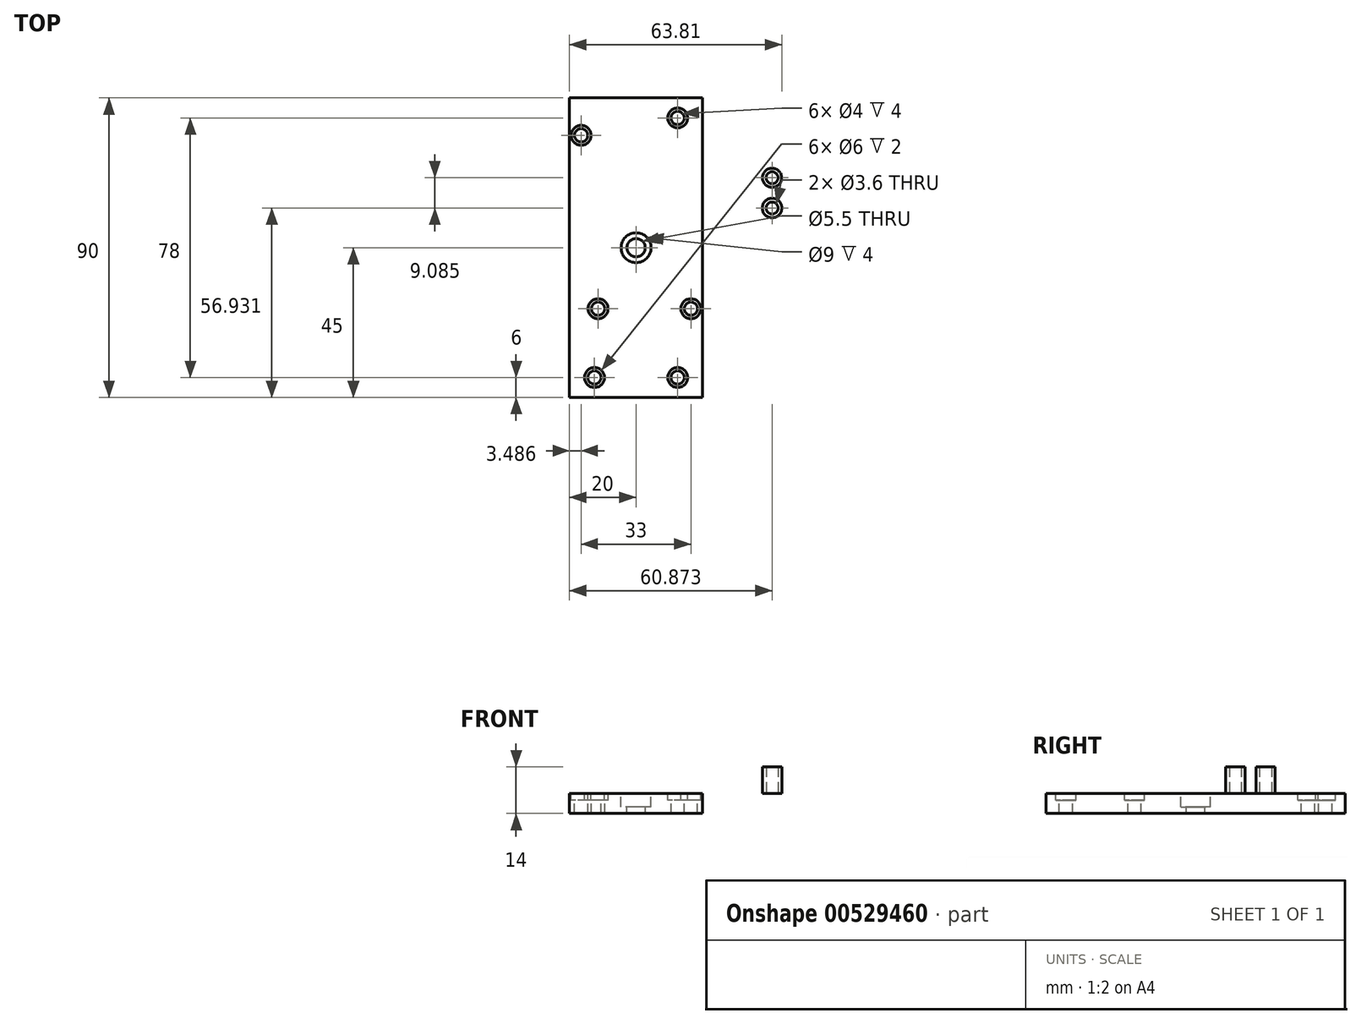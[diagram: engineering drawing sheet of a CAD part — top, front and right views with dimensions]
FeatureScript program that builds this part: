
annotation { "Feature Type Name" : "Feature", "Feature Type Description" : "" }
export const myFeature = defineFeature(function(context is Context, id is Id, definition is map)
    precondition{}
    {
        {
            assignVariable(context, id + "F0", {"name" : "base", "anyValue" : 6});
        }
        {
            assignVariable(context, id + "F1", {"name" : "pilar_d", "anyValue" : 6});
        }
        {
            var Q0;
            Q0=qCreatedBy(makeId("Top.planeOp"),FACE);
            var sketch = newSketch(context, id + "F2", { "sketchPlane" : qUnion([Q0])});
            skLineSegment(sketch, "E0.bottom", {"start": v(-20, 45) * mm, "end": v(20, 45) * mm});
            skLineSegment(sketch, "E0.top", {"start": v(-20, -45) * mm, "end": v(20, -45) * mm});
            skLineSegment(sketch, "E0.left", {"start": v(-20, 45) * mm, "end": v(-20, -45) * mm});
            skLineSegment(sketch, "E0.right", {"start": v(20, 45) * mm, "end": v(20, -45) * mm});
            skPoint(sketch, "E0.middle", {"position": v(0, 0) * mm});
            skLineSegment(sketch, "E1.bottom", {"start": v(12.5, 39) * mm, "end": v(-12.5, 39) * mm, "construction": true});
            skLineSegment(sketch, "E1.top", {"start": v(12.5, -39) * mm, "end": v(-12.5, -39) * mm, "construction": true});
            skLineSegment(sketch, "E1.left", {"start": v(12.5, 39) * mm, "end": v(12.5, -39) * mm, "construction": true});
            skLineSegment(sketch, "E1.right", {"start": v(-12.5, 39) * mm, "end": v(-12.5, -39) * mm, "construction": true});
            skLineSegment(sketch, "E2", {"start": v(-11.41, -18.33) * mm, "end": v(16.49, -18.33) * mm, "construction": true});
            skLineSegment(sketch, "E3", {"start": v(-11.41, -18.33) * mm, "end": v(-11.41, 33.77) * mm, "construction": true});
            skLineSegment(sketch, "E4", {"start": v(-11.41, 33.77) * mm, "end": v(-16.51, 33.77) * mm, "construction": true});
            skCircle(sketch, "E5", {"center": v(0, 0) * mm, "radius": 15 * mm});
            skCircle(sketch, "E6", {"center": v(40.87, 21.02) * mm, "radius": 2.88 * mm});
            skCircle(sketch, "E7", {"center": v(40.87, 11.93) * mm, "radius": 2.94 * mm});
            skLineSegment(sketch, "E8", {"start": v(40.87, 45.46) * mm, "end": v(40.87, -2.42) * mm, "construction": true});
            skSolve(sketch);
        }
        {
            var Q0;
            Q0=qCreatedBy(makeId("Top.planeOp"),FACE);
            var sketch = newSketch(context, id + "F3", { "sketchPlane" : qUnion([Q0])});
            skCircle(sketch, "E9", {"center": v(12.5, 39) * mm, "radius": 3 * mm});
            skCircle(sketch, "E10", {"center": v(12.5, -39) * mm, "radius": 3 * mm});
            skCircle(sketch, "E11", {"center": v(-12.5, -39) * mm, "radius": 3 * mm});
            skSolve(sketch);
        }
        {
            var Q0;
            Q0=qCreatedBy(makeId("Top.planeOp"),FACE);
            var sketch = newSketch(context, id + "F4", { "sketchPlane" : qUnion([Q0])});
            skCircle(sketch, "E12", {"center": v(16.49, -18.33) * mm, "radius": 3 * mm});
            skCircle(sketch, "E13", {"center": v(-11.41, -18.33) * mm, "radius": 3 * mm});
            skCircle(sketch, "E14", {"center": v(-16.51, 33.77) * mm, "radius": 3 * mm});
            skSolve(sketch);
        }
        {
            var Q0;
            Q0=makeQuery(id+"F2.imprint","IMPRINT",FACE,{"disambiguationData":[TD([[makeQuery(id+"F2.imprint","IMPRINT",EDGE,{"derivedFrom":sQuery(id+"F2.wireOp",EDGE,"E0.bottom")}),-1.0]])]});
            var Q1;
            Q1=makeQuery(id+"F2.imprint","IMPRINT",FACE,{"disambiguationData":[TD([[makeQuery(id+"F2.imprint","IMPRINT",EDGE,{"derivedFrom":sQuery(id+"F2.wireOp",EDGE,"E5")}),1.0]])]});
            extrude(context, id + "F5", {"entities" : qUnion([Q0, Q1]), "oppositeDirection" : true, "depth" : (getVariable(context, 'base')) * mm, "offsetDistance" : 25 * mm});
        }
        {
            var Q0;
            Q0=sQuery(id+"F2.wireOp",VERTEX,"E0.middle");
            var Q1;
            Q1=makeQuery(id+"F5.opExtrude","SWEPT_BODY",BODY,{"disambiguationData":[OSD([sQuery(id+"F2.wireOp",EDGE,"E0.bottom"),sQuery(id+"F2.wireOp",EDGE,"E0.top"),sQuery(id+"F2.wireOp",EDGE,"E0.left"),sQuery(id+"F2.wireOp",EDGE,"E0.right")])]});
            hole(context, id + "F6", {"style" : HoleStyle.C_BORE, "endStyle" : HoleEndStyle.BLIND, "holeDiameter" : 5.5 * mm, "cBoreDiameter" : 9 * mm, "cBoreDepth" : 4 * mm, "majorDiameter" : 5 * mm, "holeDepth" : 30 * mm, "isTappedThrough" : true, "tappedDepth" : 10.5 * mm, "tapClearance" : 3, "locations" : qUnion([Q0]), "scope" : qUnion([Q1])});
        }
        {
            var Q0;
            Q0=sQuery(id+"F2.wireOp",VERTEX,"E1.left.start");
            var Q1;
            Q1=sQuery(id+"F2.wireOp",VERTEX,"E4.end");
            var Q2;
            Q2=sQuery(id+"F4.wireOp",VERTEX,"E12.center");
            var Q3;
            Q3=sQuery(id+"F2.wireOp",VERTEX,"E2.start");
            var Q4;
            Q4=sQuery(id+"F3.wireOp",VERTEX,"E11.center");
            var Q5;
            Q5=sQuery(id+"F3.wireOp",VERTEX,"E10.center");
            var Q6;
            Q6=makeQuery(id+"F5.opExtrude","SWEPT_BODY",BODY,{"disambiguationData":[OSD([sQuery(id+"F2.wireOp",EDGE,"E0.bottom"),sQuery(id+"F2.wireOp",EDGE,"E0.top"),sQuery(id+"F2.wireOp",EDGE,"E0.left"),sQuery(id+"F2.wireOp",EDGE,"E0.right")])]});
            hole(context, id + "F7", {"style" : HoleStyle.C_BORE, "endStyle" : HoleEndStyle.BLIND, "holeDiameter" : 4 * mm, "cBoreDiameter" : (getVariable(context, 'pilar_d')) * mm, "cBoreDepth" : 2 * mm, "majorDiameter" : 5 * mm, "holeDepth" : 30 * mm, "isTappedThrough" : true, "tappedDepth" : 10.5 * mm, "tapClearance" : 3, "locations" : qUnion([Q0, Q1, Q2, Q3, Q4, Q5]), "scope" : qUnion([Q6])});
        }
        {
            var Q0;
            Q0=makeQuery(id+"F2.imprint","IMPRINT",FACE,{"disambiguationData":[TD([[makeQuery(id+"F2.imprint","IMPRINT",EDGE,{"derivedFrom":sQuery(id+"F2.wireOp",EDGE,"UOS81fSf-6cRj-C8Fn-cniU-Lerr64UJDQUZ")}),1.0]])]});
            var Q1;
            Q1=makeQuery(id+"F2.imprint","IMPRINT",FACE,{"disambiguationData":[TD([[makeQuery(id+"F2.imprint","IMPRINT",EDGE,{"derivedFrom":sQuery(id+"F2.wireOp",EDGE,"Zf9gqeoR-ahuc-C4oU-WhAM-6mYbWsj3ajmr")}),1.0]])]});
            var Q2;
            Q2=makeQuery(id+"F2.imprint","IMPRINT",FACE,{"disambiguationData":[TD([[makeQuery(id+"F2.imprint","IMPRINT",EDGE,{"derivedFrom":sQuery(id+"F2.wireOp",EDGE,"E6")}),1.0]])]});
            var Q3;
            Q3=makeQuery(id+"F2.imprint","IMPRINT",FACE,{"disambiguationData":[TD([[makeQuery(id+"F2.imprint","IMPRINT",EDGE,{"derivedFrom":sQuery(id+"F2.wireOp",EDGE,"E7")}),1.0]])]});
            extrude(context, id + "F8", {"entities" : qUnion([Q0, Q1, Q2, Q3]), "depth" : 8 * mm, "offsetDistance" : 25 * mm});
        }
        {
            var Q0;
            Q0=sQuery(id+"F2.wireOp",VERTEX,"UOS81fSf-6cRj-C8Fn-cniU-Lerr64UJDQUZ.center");
            var Q1;
            Q1=sQuery(id+"F2.wireOp",VERTEX,"E7.center");
            var Q2;
            Q2=sQuery(id+"F2.wireOp",VERTEX,"E6.center");
            var Q3;
            Q3=sQuery(id+"F2.wireOp",VERTEX,"Zf9gqeoR-ahuc-C4oU-WhAM-6mYbWsj3ajmr.center");
            var Q4;
            Q4=makeQuery(id+"F8.opExtrude","SWEPT_BODY",BODY,{"disambiguationData":[OSD([sQuery(id+"F2.wireOp",EDGE,"UOS81fSf-6cRj-C8Fn-cniU-Lerr64UJDQUZ")])]});
            var Q5;
            Q5=makeQuery(id+"F8.opExtrude","SWEPT_BODY",BODY,{"disambiguationData":[OSD([sQuery(id+"F2.wireOp",EDGE,"E7")])]});
            var Q6;
            Q6=makeQuery(id+"F8.opExtrude","SWEPT_BODY",BODY,{"disambiguationData":[OSD([sQuery(id+"F2.wireOp",EDGE,"E6")])]});
            var Q7;
            Q7=makeQuery(id+"F8.opExtrude","SWEPT_BODY",BODY,{"disambiguationData":[OSD([sQuery(id+"F2.wireOp",EDGE,"Zf9gqeoR-ahuc-C4oU-WhAM-6mYbWsj3ajmr")])]});
            hole(context, id + "F9", {"style" : HoleStyle.SIMPLE, "endStyle" : HoleEndStyle.BLIND, "oppositeDirection" : true, "holeDiameter" : 3.6 * mm, "majorDiameter" : 5 * mm, "holeDepth" : 30 * mm, "isTappedThrough" : true, "tappedDepth" : 10.5 * mm, "tapClearance" : 3, "locations" : qUnion([Q0, Q1, Q2, Q3]), "scope" : qUnion([Q4, Q5, Q6, Q7])});
        }
    });
